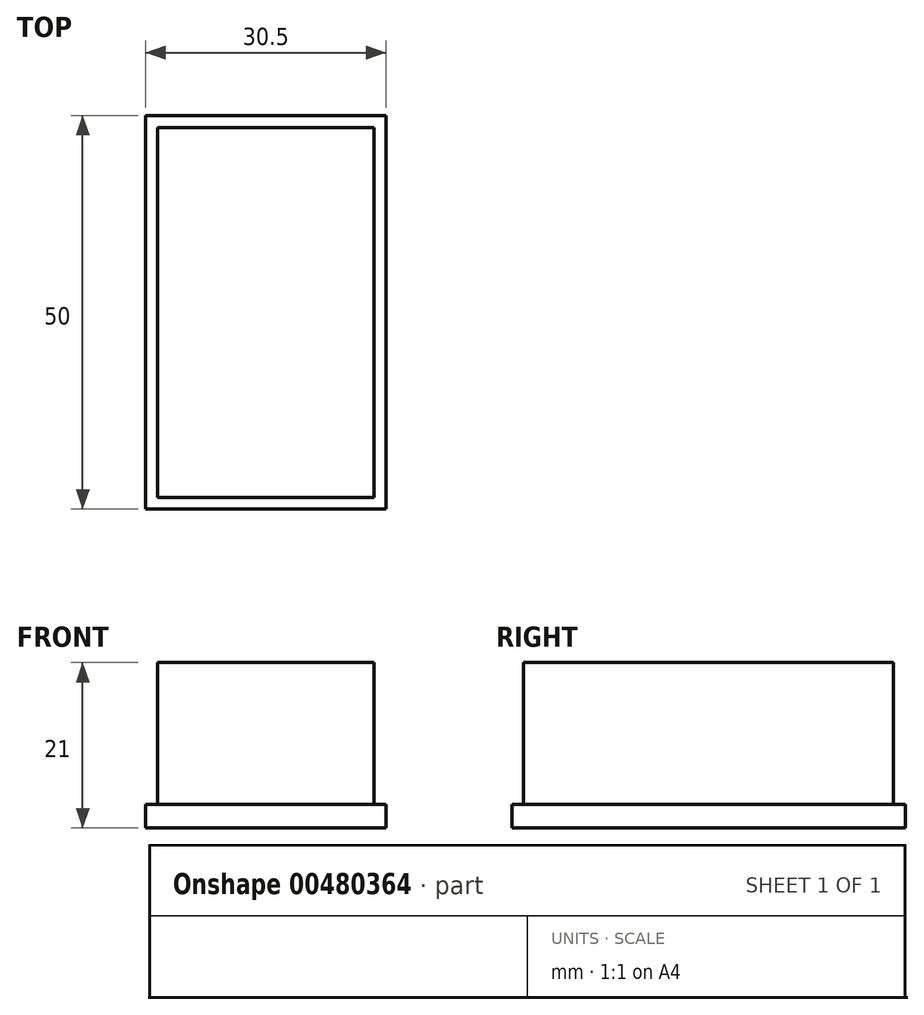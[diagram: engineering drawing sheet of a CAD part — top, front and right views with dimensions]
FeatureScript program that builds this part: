
annotation { "Feature Type Name" : "Feature", "Feature Type Description" : "" }
export const myFeature = defineFeature(function(context is Context, id is Id, definition is map)
    precondition{}
    {
        {
            var Q0;
            Q0=qCreatedBy(makeId("Top.planeOp"),FACE);
            var sketch = newSketch(context, id + "F0", { "sketchPlane" : qUnion([Q0])});
            skLineSegment(sketch, "E0.bottom", {"start": v(13.75, -23.5) * mm, "end": v(-13.75, -23.5) * mm});
            skLineSegment(sketch, "E0.top", {"start": v(13.75, 23.5) * mm, "end": v(-13.75, 23.5) * mm});
            skLineSegment(sketch, "E0.left", {"start": v(13.75, -23.5) * mm, "end": v(13.75, 23.5) * mm});
            skLineSegment(sketch, "E0.right", {"start": v(-13.75, -23.5) * mm, "end": v(-13.75, 23.5) * mm});
            skPoint(sketch, "E0.middle", {"position": v(0, 0) * mm});
            skLineSegment(sketch, "E1.bottom", {"start": v(15.25, -25) * mm, "end": v(-15.25, -25) * mm});
            skLineSegment(sketch, "E1.top", {"start": v(15.25, 25) * mm, "end": v(-15.25, 25) * mm});
            skLineSegment(sketch, "E1.left", {"start": v(15.25, -25) * mm, "end": v(15.25, 25) * mm});
            skLineSegment(sketch, "E1.right", {"start": v(-15.25, -25) * mm, "end": v(-15.25, 25) * mm});
            skSolve(sketch);
        }
        {
            var Q0;
            Q0=makeQuery(id+"F0.imprint","IMPRINT",FACE,{"disambiguationData":[TD([[makeQuery(id+"F0.imprint","IMPRINT",EDGE,{"derivedFrom":sQuery(id+"F0.wireOp",EDGE,"E0.bottom")}),-1.0]])]});
            extrude(context, id + "F1", {"entities" : qUnion([Q0]), "depth" : 18 * mm, "offsetDistance" : 25 * mm});
        }
        {
            var Q0;
            Q0=makeQuery(id+"F0.imprint","IMPRINT",FACE,{"disambiguationData":[TD([[makeQuery(id+"F0.imprint","IMPRINT",EDGE,{"derivedFrom":sQuery(id+"F0.wireOp",EDGE,"E0.bottom")}),-1.0]])]});
            var Q1;
            Q1=makeQuery(id+"F0.imprint","IMPRINT",FACE,{"disambiguationData":[TD([[makeQuery(id+"F0.imprint","IMPRINT",EDGE,{"derivedFrom":sQuery(id+"F0.wireOp",EDGE,"E0.bottom")}),1.0]])]});
            extrude(context, id + "F2", {"entities" : qUnion([Q0, Q1]), "operationType" : NewBodyOperationType.ADD, "oppositeDirection" : true, "depth" : 3 * mm, "offsetDistance" : 25 * mm});
        }
    });
